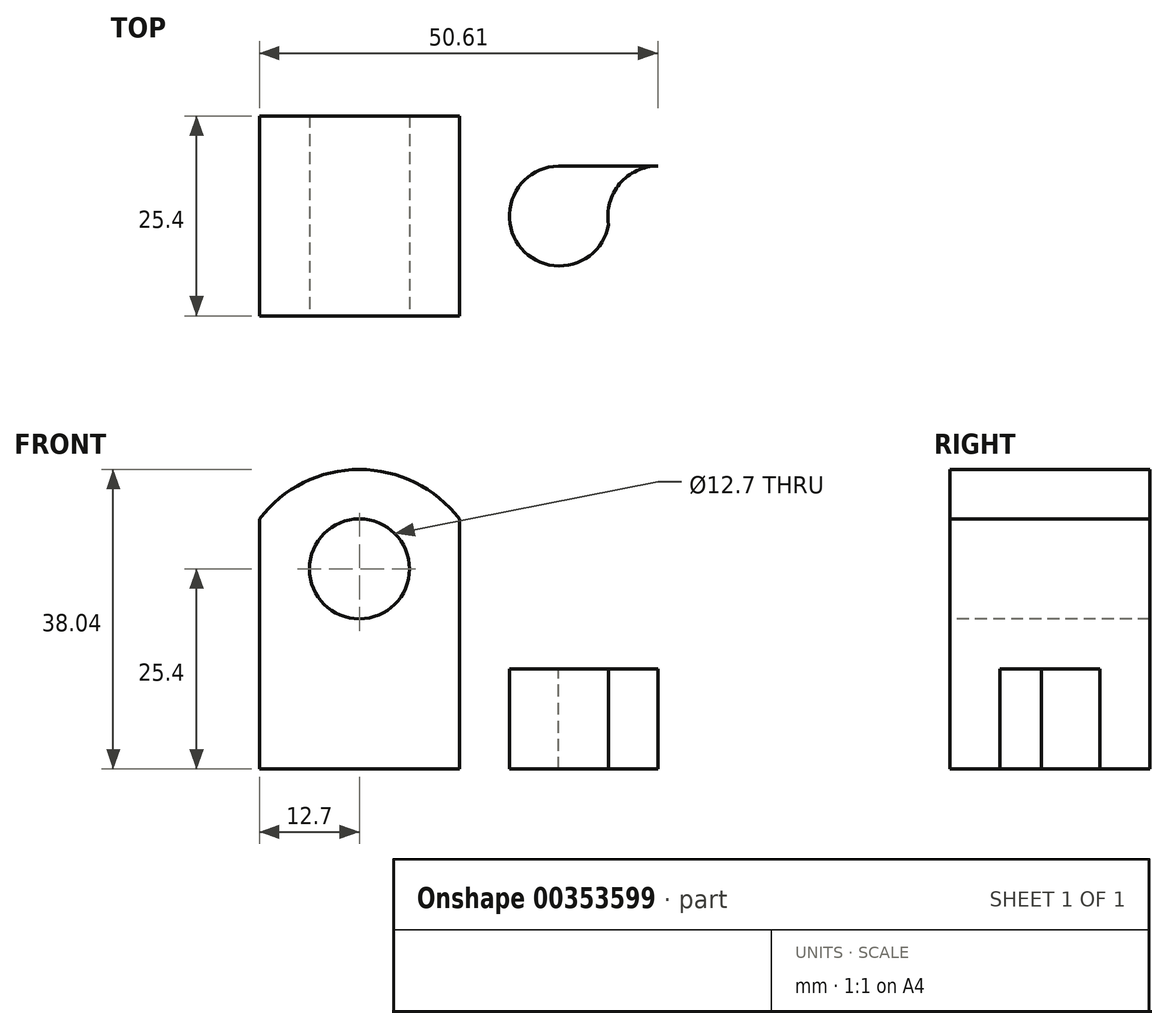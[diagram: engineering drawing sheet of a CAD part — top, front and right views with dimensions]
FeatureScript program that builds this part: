
annotation { "Feature Type Name" : "Feature", "Feature Type Description" : "" }
export const myFeature = defineFeature(function(context is Context, id is Id, definition is map)
    precondition{}
    {
        {
            var Q0;
            Q0=qCreatedBy(makeId("Front.planeOp"),FACE);
            var sketch = newSketch(context, id + "F0", { "sketchPlane" : qUnion([Q0])});
            skLineSegment(sketch, "E0", {"start": v(0, 0) * mm, "end": v(0, 38.1) * mm});
            skLineSegment(sketch, "E1", {"start": v(0, 38.1) * mm, "end": v(25.4, 38.1) * mm});
            skLineSegment(sketch, "E2", {"start": v(25.4, 38.1) * mm, "end": v(25.4, 12.7) * mm});
            skLineSegment(sketch, "E3", {"start": v(25.4, 12.7) * mm, "end": v(63.5, 12.7) * mm});
            skLineSegment(sketch, "E4", {"start": v(63.5, 12.7) * mm, "end": v(63.5, 0) * mm});
            skLineSegment(sketch, "E5", {"start": v(63.5, 0) * mm, "end": v(0, 0) * mm});
            skSolve(sketch);
        }
        {
            var Q0;
            Q0=makeQuery(id+"F0.imprint","IMPRINT",FACE,{"disambiguationData":[TD([[makeQuery(id+"F0.imprint","IMPRINT",EDGE,{"derivedFrom":sQuery(id+"F0.wireOp",EDGE,"E0")}),-1.0]])]});
            extrude(context, id + "F1", {"entities" : qUnion([Q0]), "depth" : 25.4 * mm});
        }
        {
            var Q0;
            Q0=makeQuery(id+"F1.opExtrude","CAP_FACE",FACE,{"disambiguationData":[OSD([sQuery(id+"F0.wireOp",EDGE,"E0"),sQuery(id+"F0.wireOp",EDGE,"E1"),sQuery(id+"F0.wireOp",EDGE,"E2"),sQuery(id+"F0.wireOp",EDGE,"E3"),sQuery(id+"F0.wireOp",EDGE,"E4"),sQuery(id+"F0.wireOp",EDGE,"E5")])],"isStart":false});
            var sketch = newSketch(context, id + "F2", { "sketchPlane" : qUnion([Q0])});
            skLineSegment(sketch, "E6", {"start": v(0, 31.75) * mm, "end": v(0, 38.1) * mm});
            skLineSegment(sketch, "E7", {"start": v(0, 38.1) * mm, "end": v(25.4, 38.1) * mm});
            skLineSegment(sketch, "E8", {"start": v(25.4, 38.1) * mm, "end": v(25.4, 31.75) * mm});
            skCircle(sketch, "E9", {"center": v(12.7, 25.4) * mm, "radius": 6.35 * mm});
            skArc(sketch, "E10", {"start": v(25.4, 31.75) * mm, "mid": v(12.7, 38.04) * mm, "end": v(0, 31.75) * mm});
            skSolve(sketch);
        }
        {
            var Q0;
            Q0=makeQuery(id+"F2.imprint","IMPRINT",FACE,{"disambiguationData":[TD([[makeQuery(id+"F2.imprint","IMPRINT",EDGE,{"derivedFrom":sQuery(id+"F2.wireOp",EDGE,"E6")}),-1.0]])]});
            var Q1;
            Q1=makeQuery(id+"F2.imprint","IMPRINT",FACE,{"disambiguationData":[TD([[makeQuery(id+"F2.imprint","IMPRINT",EDGE,{"derivedFrom":sQuery(id+"F2.wireOp",EDGE,"E9")}),1.0]])]});
            extrude(context, id + "F3", {"entities" : qUnion([Q0, Q1]), "operationType" : NewBodyOperationType.REMOVE, "oppositeDirection" : true, "depth" : 25.4 * mm});
        }
        {
            var Q0;
            Q0=makeQuery(id+"F1.opExtrude","SWEPT_FACE",FACE,{"disambiguationData":[OSD([sQuery(id+"F0.wireOp",EDGE,"E3")])]});
            var sketch = newSketch(context, id + "F4", { "sketchPlane" : qUnion([Q0])});
            skArc(sketch, "E11", {"start": v(50.8, -25.4) * mm, "mid": v(63.31, -12.7) * mm, "end": v(50.8, 0) * mm});
            skLineSegment(sketch, "E12", {"start": v(50.8, 0) * mm, "end": v(63.5, 0) * mm});
            skLineSegment(sketch, "E13", {"start": v(63.5, 0) * mm, "end": v(63.5, -25.4) * mm});
            skLineSegment(sketch, "E14", {"start": v(63.5, -25.4) * mm, "end": v(50.8, -25.4) * mm});
            skSolve(sketch);
        }
        {
            var Q0;
            Q0=makeQuery(id+"F4.imprint","IMPRINT",FACE,{"disambiguationData":[TD([[makeQuery(id+"F4.imprint","IMPRINT",EDGE,{"derivedFrom":sQuery(id+"F4.wireOp",EDGE,"E11")}),-1.0]])]});
            extrude(context, id + "F5", {"entities" : qUnion([Q0]), "operationType" : NewBodyOperationType.REMOVE, "oppositeDirection" : true, "depth" : 25.4 * mm});
        }
        {
            var Q0;
            Q0=makeQuery(id+"F1.opExtrude","SWEPT_FACE",FACE,{"disambiguationData":[OSD([sQuery(id+"F0.wireOp",EDGE,"E3")])]});
            var sketch = newSketch(context, id + "F6", { "sketchPlane" : qUnion([Q0])});
            skCircle(sketch, "E15", {"center": v(38.1, -12.7) * mm, "radius": 6.35 * mm});
            skCircle(sketch, "E16", {"center": v(50.61, -12.7) * mm, "radius": 6.35 * mm});
            skLineSegment(sketch, "E17", {"start": v(37.96, -6.35) * mm, "end": v(50.61, -6.35) * mm});
            skLineSegment(sketch, "E18", {"start": v(38.23, -19.05) * mm, "end": v(50.61, -19.05) * mm});
            skSolve(sketch);
        }
        {
            var Q0;
            {var subQ1=sQuery(id+"F6.wireOp",EDGE,"E15");var subQ5=sQuery(id+"F6.wireOp",EDGE,"E17");var subQ7=makeQuery(id+"F6.imprint","INTERSECT",VERTEX,{"disambiguationData":[OD(1.0)],"derivedFrom":[subQ1,subQ5]});Q0=makeQuery(id+"F6.imprint","IMPRINT",FACE,{"disambiguationData":[TD([[makeQuery(id+"F6.imprint","IMPRINT",EDGE,{"disambiguationData":[TD([[subQ7,1.0]])],"derivedFrom":subQ1}),1.0]])]});}
            var Q1;
            {var subQ0=sQuery(id+"F6.wireOp",EDGE,"E16");var subQ1=sQuery(id+"F6.wireOp",EDGE,"E15");var subQ2=makeQuery(id+"F6.imprint","INTERSECT",VERTEX,{"disambiguationData":[OD(0.0)],"derivedFrom":[subQ1,subQ0]});Q1=makeQuery(id+"F6.imprint","IMPRINT",FACE,{"disambiguationData":[TD([[makeQuery(id+"F6.imprint","IMPRINT",EDGE,{"disambiguationData":[TD([[subQ2,1.0]])],"derivedFrom":subQ1}),-1.0]])]});}
            var Q2;
            {var subQ0=sQuery(id+"F6.wireOp",EDGE,"E18");Q2=makeQuery(id+"F6.imprint","IMPRINT",FACE,{"disambiguationData":[TD([[makeQuery(id+"F6.imprint","IMPRINT",EDGE,{"derivedFrom":subQ0}),1.0]])]});}
            var Q3;
            {var subQ0=sQuery(id+"F6.wireOp",EDGE,"E17");var subQ1=sQuery(id+"F6.wireOp",EDGE,"E15");var subQ2=makeQuery(id+"F6.imprint","INTERSECT",VERTEX,{"disambiguationData":[OD(1.0)],"derivedFrom":[subQ1,subQ0]});Q3=makeQuery(id+"F6.imprint","IMPRINT",FACE,{"disambiguationData":[TD([[makeQuery(id+"F6.imprint","IMPRINT",EDGE,{"disambiguationData":[TD([[subQ2,1.0]])],"derivedFrom":subQ1}),-1.0]])]});}
            var Q4;
            {var subQ0=sQuery(id+"F6.wireOp",EDGE,"E16");var subQ1=sQuery(id+"F6.wireOp",EDGE,"E15");var subQ2=makeQuery(id+"F6.imprint","INTERSECT",VERTEX,{"disambiguationData":[OD(0.0)],"derivedFrom":[subQ1,subQ0]});Q4=makeQuery(id+"F6.imprint","IMPRINT",FACE,{"disambiguationData":[TD([[makeQuery(id+"F6.imprint","IMPRINT",EDGE,{"disambiguationData":[TD([[subQ2,1.0]])],"derivedFrom":subQ1}),1.0]])]});}
            extrude(context, id + "F7", {"entities" : qUnion([Q0, Q1, Q2, Q3, Q4]), "operationType" : NewBodyOperationType.REMOVE, "oppositeDirection" : true, "depth" : 25.4 * mm});
        }
    });
